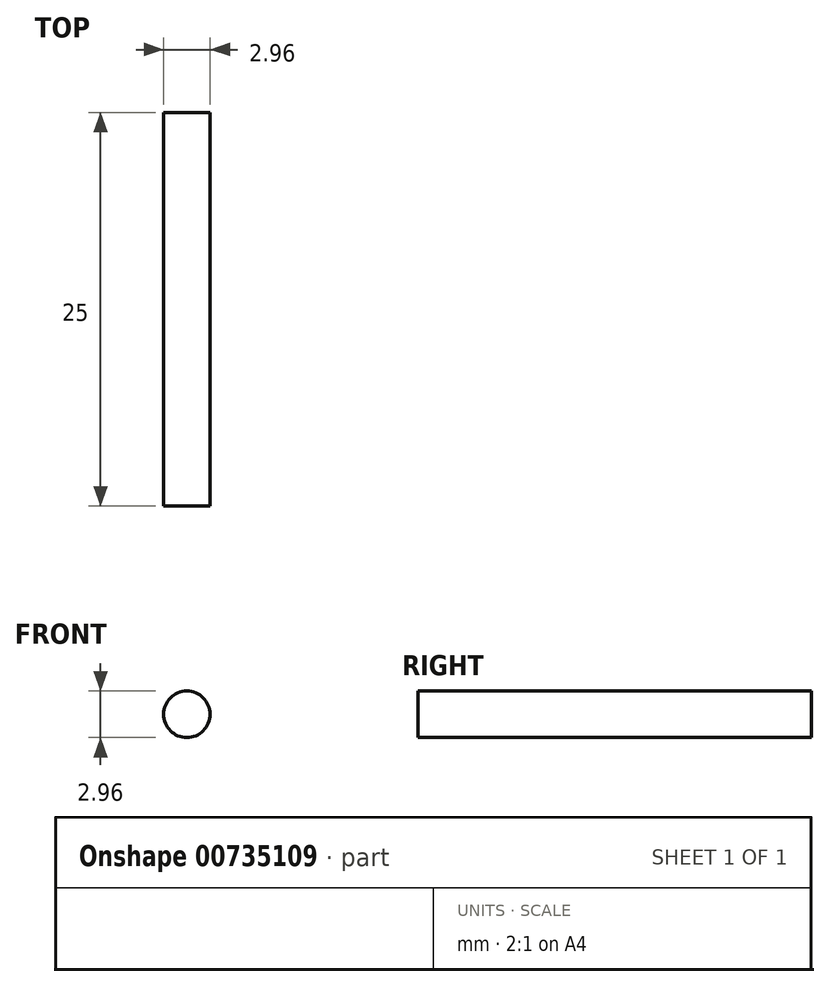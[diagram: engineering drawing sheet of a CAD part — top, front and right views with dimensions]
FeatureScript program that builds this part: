
annotation { "Feature Type Name" : "Feature", "Feature Type Description" : "" }
export const myFeature = defineFeature(function(context is Context, id is Id, definition is map)
    precondition{}
    {
        {
            var Q0;
            Q0=qCreatedBy(makeId("Front.planeOp"),FACE);
            var sketch = newSketch(context, id + "F0", { "sketchPlane" : qUnion([Q0])});
            skCircle(sketch, "E0", {"center": v(0, 0) * mm, "radius": 1.48 * mm});
            skSolve(sketch);
        }
        {
            var Q0;
            Q0 = qSketchRegion(id + "F0", true);
            extrude(context, id + "F1", {"entities" : qUnion([Q0]), "oppositeDirection" : true, "depth" : 25 * mm, "offsetDistance" : 25 * mm});
        }
    });
